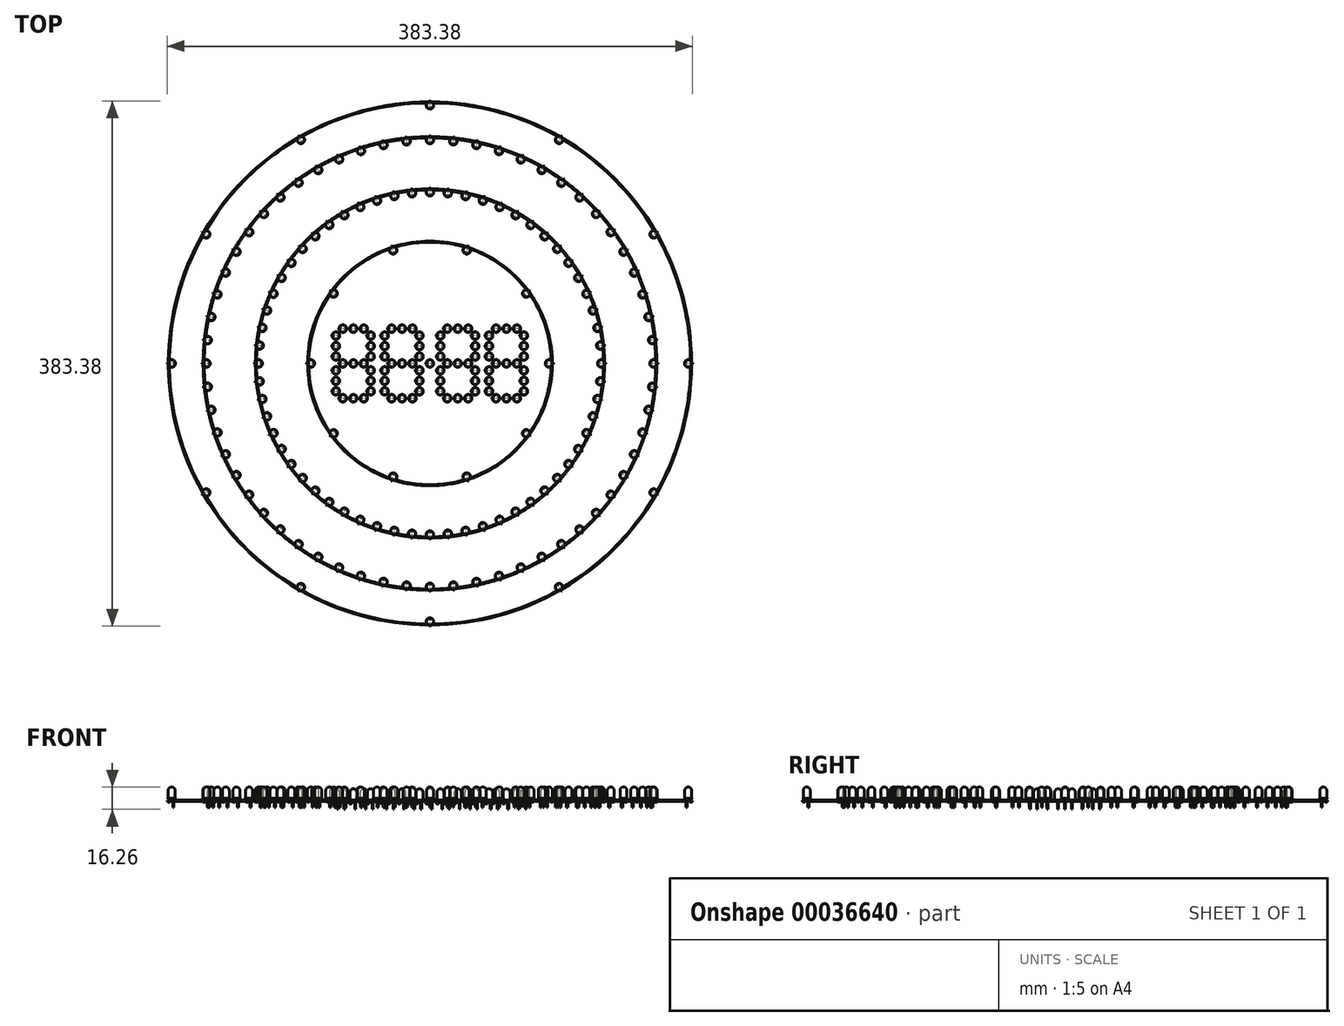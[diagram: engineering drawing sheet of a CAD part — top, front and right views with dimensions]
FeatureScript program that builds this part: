
annotation { "Feature Type Name" : "Feature", "Feature Type Description" : "" }
export const myFeature = defineFeature(function(context is Context, id is Id, definition is map)
    precondition{}
    {
        {
            var Q0;
            Q0=qCreatedBy(makeId("Top.planeOp"),FACE);
            var sketch = newSketch(context, id + "F0", { "sketchPlane" : qUnion([Q0])});
            skLineSegment(sketch, "E0", {"start": v(0, 0) * mm, "end": v(-2.8, 0) * mm});
            skLineSegment(sketch, "E1", {"start": v(-2.8, 0) * mm, "end": v(-2.8, 0.5) * mm});
            skLineSegment(sketch, "E2", {"start": v(-2.8, 0.5) * mm, "end": v(-2.54, 0.5) * mm});
            skLineSegment(sketch, "E3", {"start": v(-2.54, 0.5) * mm, "end": v(-2.54, 6.1) * mm});
            skLineSegment(sketch, "E4", {"start": v(0, 8.64) * mm, "end": v(0, 8.64) * mm});
            skLineSegment(sketch, "E5", {"start": v(0, 8.64) * mm, "end": v(0, 0) * mm});
            skPoint(sketch, "E6.visualSharp", {"position": v(-2.54, 8.64) * mm});
            skArc(sketch, "E6.filletArc", {"start": v(0, 8.64) * mm, "mid": v(-1.8, 7.9) * mm, "end": v(-2.54, 6.1) * mm});
            skSolve(sketch);
        }
        {
            var Q0;
            Q0=makeQuery(id+"F0.imprint","IMPRINT",FACE,{"disambiguationData":[TD([[makeQuery(id+"F0.imprint","IMPRINT",EDGE,{"derivedFrom":sQuery(id+"F0.wireOp",EDGE,"E0")}),-1.0]])]});
            var Q1;
            Q1=sQuery(id+"F0.wireOp",EDGE,"E5");
            revolve(context, id + "F1", {"entities" : qUnion([Q0]), "axis" : qUnion([Q1]), "revolveType" : RevolveType.FULL});
        }
        {
            var Q0;
            Q0=makeQuery(id+"F1.opRevolve","SWEPT_FACE",FACE,{"disambiguationData":[OSD([sQuery(id+"F0.wireOp",EDGE,"E0")])]});
            var sketch = newSketch(context, id + "F2", { "sketchPlane" : qUnion([Q0])});
            skLineSegment(sketch, "E7", {"start": v(0, 0) * mm, "end": v(0.89, 0) * mm, "construction": true});
            skLineSegment(sketch, "E8.bottom", {"start": v(0.89, 0.38) * mm, "end": v(1.65, 0.38) * mm});
            skLineSegment(sketch, "E8.top", {"start": v(0.89, -0.38) * mm, "end": v(1.65, -0.38) * mm});
            skLineSegment(sketch, "E8.left", {"start": v(0.89, 0.38) * mm, "end": v(0.89, -0.38) * mm});
            skLineSegment(sketch, "E8.right", {"start": v(1.65, 0.38) * mm, "end": v(1.65, -0.38) * mm});
            skLineSegment(sketch, "E9.MirrorCS", {"start": v(-0.89, 0.38) * mm, "end": v(-0.89, -0.38) * mm});
            skLineSegment(sketch, "E10.MirrorCS", {"start": v(-0.89, 0.38) * mm, "end": v(-1.65, 0.38) * mm});
            skLineSegment(sketch, "E11.MirrorCS", {"start": v(-1.65, 0.38) * mm, "end": v(-1.65, -0.38) * mm});
            skLineSegment(sketch, "E12.MirrorCS", {"start": v(-0.89, -0.38) * mm, "end": v(-1.65, -0.38) * mm});
            skSolve(sketch);
        }
        {
            var Q0;
            Q0=makeQuery(id+"F2.imprint","IMPRINT",FACE,{"disambiguationData":[TD([[makeQuery(id+"F2.imprint","IMPRINT",EDGE,{"derivedFrom":sQuery(id+"F2.wireOp",EDGE,"E9.MirrorCS")}),-1.0]])]});
            extrude(context, id + "F3", {"entities" : qUnion([Q0]), "operationType" : NewBodyOperationType.ADD, "depth" : 1.27 * mm});
        }
        {
            var Q0;
            Q0=makeQuery(id+"F2.imprint","IMPRINT",FACE,{"disambiguationData":[TD([[makeQuery(id+"F2.imprint","IMPRINT",EDGE,{"derivedFrom":sQuery(id+"F2.wireOp",EDGE,"E8.bottom")}),-1.0]])]});
            extrude(context, id + "F4", {"entities" : qUnion([Q0]), "operationType" : NewBodyOperationType.ADD, "depth" : 6.35 * mm});
        }
        {
            var Q0;
            Q0=qCreatedBy(makeId("Front.planeOp"),FACE);
            var sketch = newSketch(context, id + "F5", { "sketchPlane" : qUnion([Q0])});
            skCircle(sketch, "E13", {"center": v(-88.9, 0) * mm, "radius": 0.4 * mm});
            skCircle(sketch, "E14", {"center": v(-127, 0) * mm, "radius": 0.4 * mm});
            skCircle(sketch, "E15", {"center": v(-165.1, 0) * mm, "radius": 0.4 * mm});
            skCircle(sketch, "E16", {"center": v(-190.5, 0) * mm, "radius": 0.4 * mm});
            skLineSegment(sketch, "E17", {"start": v(0, 44.63) * mm, "end": v(0, 0) * mm, "construction": true});
            skLineSegment(sketch, "E18", {"start": v(0, 0) * mm, "end": v(0, -40.21) * mm, "construction": true});
            skSolve(sketch);
        }
        {
            var Q0;
            Q0=makeQuery(id+"F5.imprint","IMPRINT",FACE,{"disambiguationData":[TD([[makeQuery(id+"F5.imprint","IMPRINT",EDGE,{"derivedFrom":sQuery(id+"F5.wireOp",EDGE,"E16")}),1.0]])]});
            var Q1;
            Q1=makeQuery(id+"F5.imprint","IMPRINT",FACE,{"disambiguationData":[TD([[makeQuery(id+"F5.imprint","IMPRINT",EDGE,{"derivedFrom":sQuery(id+"F5.wireOp",EDGE,"E15")}),1.0]])]});
            var Q2;
            Q2=makeQuery(id+"F5.imprint","IMPRINT",FACE,{"disambiguationData":[TD([[makeQuery(id+"F5.imprint","IMPRINT",EDGE,{"derivedFrom":sQuery(id+"F5.wireOp",EDGE,"E14")}),1.0]])]});
            var Q3;
            Q3=makeQuery(id+"F5.imprint","IMPRINT",FACE,{"disambiguationData":[TD([[makeQuery(id+"F5.imprint","IMPRINT",EDGE,{"derivedFrom":sQuery(id+"F5.wireOp",EDGE,"E13")}),1.0]])]});
            var Q4;
            Q4=sQuery(id+"F5.wireOp",EDGE,"E18");
            revolve(context, id + "F6", {"entities" : qUnion([Q0, Q1, Q2, Q3]), "axis" : qUnion([Q4]), "revolveType" : RevolveType.FULL});
        }
        {
            var Q0;
            Q0=makeQuery(id+"F1.opRevolve","SWEPT_BODY",BODY,{"disambiguationData":[OSD([sQuery(id+"F0.wireOp",EDGE,"E0"),sQuery(id+"F0.wireOp",EDGE,"E1"),sQuery(id+"F0.wireOp",EDGE,"E2"),sQuery(id+"F0.wireOp",EDGE,"E3"),sQuery(id+"F0.wireOp",EDGE,"E5"),sQuery(id+"F0.wireOp",EDGE,"E6.filletArc")])]});
            var Q1;
            Q1=sQuery(id+"F0.wireOp",EDGE,"E0");
            transform(context, id + "F7", {"entities" : qUnion([Q0]), "transformType" : TransformType.ROTATION, "transformAxis" : qUnion([Q1]), "angle" : 270 * degree, "makeCopy" : false});
        }
        {
            var Q0;
            Q0=makeQuery(id+"F3.opExtrude","SWEPT_FACE",FACE,{"disambiguationData":[OSD([sQuery(id+"F2.wireOp",EDGE,"E10.MirrorCS")])]});
            var sketch = newSketch(context, id + "F8", { "sketchPlane" : qUnion([Q0])});
            skCircle(sketch, "E19", {"center": v(-2.06, -1.27) * mm, "radius": 0.4 * mm});
            skSolve(sketch);
        }
        {
            var Q0;
            Q0=makeQuery(id+"F3.opExtrude","CAP_FACE",FACE,{"disambiguationData":[OSD([sQuery(id+"F2.wireOp",EDGE,"E9.MirrorCS"),sQuery(id+"F2.wireOp",EDGE,"E10.MirrorCS"),sQuery(id+"F2.wireOp",EDGE,"E11.MirrorCS"),sQuery(id+"F2.wireOp",EDGE,"E12.MirrorCS")])],"isStart":false});
            var Q1;
            Q1=sQuery(id+"F8.wireOp",EDGE,"E19");
            revolve(context, id + "F9", {"operationType" : NewBodyOperationType.ADD, "entities" : qUnion([Q0]), "axis" : qUnion([Q1]), "revolveType" : RevolveType.ONE_DIRECTION, "oppositeDirection" : true, "angle" : 180 * degree});
        }
        {
            var Q0;
            Q0=makeQuery(id+"F1.opRevolve","SWEPT_BODY",BODY,{"disambiguationData":[OSD([sQuery(id+"F0.wireOp",EDGE,"E0"),sQuery(id+"F0.wireOp",EDGE,"E1"),sQuery(id+"F0.wireOp",EDGE,"E2"),sQuery(id+"F0.wireOp",EDGE,"E3"),sQuery(id+"F0.wireOp",EDGE,"E5"),sQuery(id+"F0.wireOp",EDGE,"E6.filletArc")])]});
            transform(context, id + "F10", {"entities" : qUnion([Q0]), "transformType" : TransformType.TRANSLATION_3D, "dx" : -86.87 * mm, "dy" : 0 * mm, "dz" : 1.27 * mm, "makeCopy" : true});
        }
        {
            var Q0;
            Q0=makeQuery(id+"F1.opRevolve","SWEPT_BODY",BODY,{"disambiguationData":[OSD([sQuery(id+"F0.wireOp",EDGE,"E0"),sQuery(id+"F0.wireOp",EDGE,"E1"),sQuery(id+"F0.wireOp",EDGE,"E2"),sQuery(id+"F0.wireOp",EDGE,"E3"),sQuery(id+"F0.wireOp",EDGE,"E5"),sQuery(id+"F0.wireOp",EDGE,"E6.filletArc")])]});
            transform(context, id + "F11", {"entities" : qUnion([Q0]), "transformType" : TransformType.TRANSLATION_3D, "dx" : -124.97 * mm, "dy" : 0 * mm, "dz" : 1.27 * mm, "makeCopy" : true});
        }
        {
            var Q0;
            Q0=makeQuery(id+"F1.opRevolve","SWEPT_BODY",BODY,{"disambiguationData":[OSD([sQuery(id+"F0.wireOp",EDGE,"E0"),sQuery(id+"F0.wireOp",EDGE,"E1"),sQuery(id+"F0.wireOp",EDGE,"E2"),sQuery(id+"F0.wireOp",EDGE,"E3"),sQuery(id+"F0.wireOp",EDGE,"E5"),sQuery(id+"F0.wireOp",EDGE,"E6.filletArc")])]});
            transform(context, id + "F12", {"entities" : qUnion([Q0]), "transformType" : TransformType.TRANSLATION_3D, "dx" : -163.07 * mm, "dy" : 0 * mm, "dz" : 1.27 * mm, "makeCopy" : true});
        }
        {
            var Q0;
            Q0=makeQuery(id+"F1.opRevolve","SWEPT_BODY",BODY,{"disambiguationData":[OSD([sQuery(id+"F0.wireOp",EDGE,"E0"),sQuery(id+"F0.wireOp",EDGE,"E1"),sQuery(id+"F0.wireOp",EDGE,"E2"),sQuery(id+"F0.wireOp",EDGE,"E3"),sQuery(id+"F0.wireOp",EDGE,"E5"),sQuery(id+"F0.wireOp",EDGE,"E6.filletArc")])]});
            transform(context, id + "F13", {"entities" : qUnion([Q0]), "transformType" : TransformType.TRANSLATION_3D, "dx" : -188.47 * mm, "dy" : 0 * mm, "dz" : 1.27 * mm, "makeCopy" : true});
        }
        {
            var Q0;
            Q0=makeQuery(id+"F10.opPattern","COPY",BODY,{"derivedFrom":makeQuery(id+"F1.opRevolve","SWEPT_BODY",BODY,{"disambiguationData":[OSD([sQuery(id+"F0.wireOp",EDGE,"E0"),sQuery(id+"F0.wireOp",EDGE,"E1"),sQuery(id+"F0.wireOp",EDGE,"E2"),sQuery(id+"F0.wireOp",EDGE,"E3"),sQuery(id+"F0.wireOp",EDGE,"E5"),sQuery(id+"F0.wireOp",EDGE,"E6.filletArc")])]}),"instanceName":"1"});
            var Q1;
            Q1=sQuery(id+"F5.wireOp",EDGE,"E17");
            circularPattern(context, id + "F14", {"entities" : qUnion([Q0]), "axis" : qUnion([Q1]), "angle" : 36 * degree, "instanceCount" : 10});
        }
        {
            var Q0;
            Q0=makeQuery(id+"F11.opPattern","COPY",BODY,{"derivedFrom":makeQuery(id+"F1.opRevolve","SWEPT_BODY",BODY,{"disambiguationData":[OSD([sQuery(id+"F0.wireOp",EDGE,"E0"),sQuery(id+"F0.wireOp",EDGE,"E1"),sQuery(id+"F0.wireOp",EDGE,"E2"),sQuery(id+"F0.wireOp",EDGE,"E3"),sQuery(id+"F0.wireOp",EDGE,"E5"),sQuery(id+"F0.wireOp",EDGE,"E6.filletArc")])]}),"instanceName":"1"});
            var Q1;
            Q1=makeQuery(id+"F12.opPattern","COPY",BODY,{"derivedFrom":makeQuery(id+"F1.opRevolve","SWEPT_BODY",BODY,{"disambiguationData":[OSD([sQuery(id+"F0.wireOp",EDGE,"E0"),sQuery(id+"F0.wireOp",EDGE,"E1"),sQuery(id+"F0.wireOp",EDGE,"E2"),sQuery(id+"F0.wireOp",EDGE,"E3"),sQuery(id+"F0.wireOp",EDGE,"E5"),sQuery(id+"F0.wireOp",EDGE,"E6.filletArc")])]}),"instanceName":"1"});
            var Q2;
            Q2=sQuery(id+"F5.wireOp",EDGE,"E17");
            circularPattern(context, id + "F15", {"entities" : qUnion([Q0, Q1]), "axis" : qUnion([Q2]), "angle" : 6 * degree, "instanceCount" : 60});
        }
        {
            var Q0;
            Q0=makeQuery(id+"F13.opPattern","COPY",BODY,{"derivedFrom":makeQuery(id+"F1.opRevolve","SWEPT_BODY",BODY,{"disambiguationData":[OSD([sQuery(id+"F0.wireOp",EDGE,"E0"),sQuery(id+"F0.wireOp",EDGE,"E1"),sQuery(id+"F0.wireOp",EDGE,"E2"),sQuery(id+"F0.wireOp",EDGE,"E3"),sQuery(id+"F0.wireOp",EDGE,"E5"),sQuery(id+"F0.wireOp",EDGE,"E6.filletArc")])]}),"instanceName":"1"});
            var Q1;
            Q1=sQuery(id+"F5.wireOp",EDGE,"E17");
            circularPattern(context, id + "F16", {"entities" : qUnion([Q0]), "axis" : qUnion([Q1]), "angle" : 30 * degree, "instanceCount" : 12});
        }
        {
            var Q0;
            Q0=makeQuery(id+"F1.opRevolve","SWEPT_BODY",BODY,{"disambiguationData":[OSD([sQuery(id+"F0.wireOp",EDGE,"E0"),sQuery(id+"F0.wireOp",EDGE,"E1"),sQuery(id+"F0.wireOp",EDGE,"E2"),sQuery(id+"F0.wireOp",EDGE,"E3"),sQuery(id+"F0.wireOp",EDGE,"E5"),sQuery(id+"F0.wireOp",EDGE,"E6.filletArc")])]});
            transform(context, id + "F17", {"entities" : qUnion([Q0]), "transformType" : TransformType.TRANSLATION_3D, "dx" : -63.5 * mm, "dy" : 0 * mm, "dz" : 0 * mm, "makeCopy" : true});
        }
        {
            var Q0;
            Q0=makeQuery(id+"F17.opPattern","COPY",BODY,{"derivedFrom":makeQuery(id+"F1.opRevolve","SWEPT_BODY",BODY,{"disambiguationData":[OSD([sQuery(id+"F0.wireOp",EDGE,"E0"),sQuery(id+"F0.wireOp",EDGE,"E1"),sQuery(id+"F0.wireOp",EDGE,"E2"),sQuery(id+"F0.wireOp",EDGE,"E3"),sQuery(id+"F0.wireOp",EDGE,"E5"),sQuery(id+"F0.wireOp",EDGE,"E6.filletArc")])]}),"instanceName":"1"});
            transform(context, id + "F18", {"entities" : qUnion([Q0]), "transformType" : TransformType.TRANSLATION_3D, "dx" : 7.62 * mm, "dy" : 0 * mm, "dz" : 0 * mm, "makeCopy" : true});
        }
        {
            var Q0;
            Q0=makeQuery(id+"F18.opPattern","COPY",BODY,{"derivedFrom":makeQuery(id+"F17.opPattern","COPY",BODY,{"derivedFrom":makeQuery(id+"F1.opRevolve","SWEPT_BODY",BODY,{"disambiguationData":[OSD([sQuery(id+"F0.wireOp",EDGE,"E0"),sQuery(id+"F0.wireOp",EDGE,"E1"),sQuery(id+"F0.wireOp",EDGE,"E2"),sQuery(id+"F0.wireOp",EDGE,"E3"),sQuery(id+"F0.wireOp",EDGE,"E5"),sQuery(id+"F0.wireOp",EDGE,"E6.filletArc")])]}),"instanceName":"1"}),"instanceName":"1"});
            transform(context, id + "F19", {"entities" : qUnion([Q0]), "transformType" : TransformType.TRANSLATION_3D, "dx" : 7.62 * mm, "dy" : 0 * mm, "dz" : 0 * mm, "makeCopy" : true});
        }
        {
            var Q0;
            Q0=makeQuery(id+"F17.opPattern","COPY",BODY,{"derivedFrom":makeQuery(id+"F1.opRevolve","SWEPT_BODY",BODY,{"disambiguationData":[OSD([sQuery(id+"F0.wireOp",EDGE,"E0"),sQuery(id+"F0.wireOp",EDGE,"E1"),sQuery(id+"F0.wireOp",EDGE,"E2"),sQuery(id+"F0.wireOp",EDGE,"E3"),sQuery(id+"F0.wireOp",EDGE,"E5"),sQuery(id+"F0.wireOp",EDGE,"E6.filletArc")])]}),"instanceName":"1"});
            var Q1;
            Q1=makeQuery(id+"F19.opPattern","COPY",BODY,{"derivedFrom":makeQuery(id+"F18.opPattern","COPY",BODY,{"derivedFrom":makeQuery(id+"F17.opPattern","COPY",BODY,{"derivedFrom":makeQuery(id+"F1.opRevolve","SWEPT_BODY",BODY,{"disambiguationData":[OSD([sQuery(id+"F0.wireOp",EDGE,"E0"),sQuery(id+"F0.wireOp",EDGE,"E1"),sQuery(id+"F0.wireOp",EDGE,"E2"),sQuery(id+"F0.wireOp",EDGE,"E3"),sQuery(id+"F0.wireOp",EDGE,"E5"),sQuery(id+"F0.wireOp",EDGE,"E6.filletArc")])]}),"instanceName":"1"}),"instanceName":"1"}),"instanceName":"1"});
            var Q2;
            Q2=makeQuery(id+"F18.opPattern","COPY",BODY,{"derivedFrom":makeQuery(id+"F17.opPattern","COPY",BODY,{"derivedFrom":makeQuery(id+"F1.opRevolve","SWEPT_BODY",BODY,{"disambiguationData":[OSD([sQuery(id+"F0.wireOp",EDGE,"E0"),sQuery(id+"F0.wireOp",EDGE,"E1"),sQuery(id+"F0.wireOp",EDGE,"E2"),sQuery(id+"F0.wireOp",EDGE,"E3"),sQuery(id+"F0.wireOp",EDGE,"E5"),sQuery(id+"F0.wireOp",EDGE,"E6.filletArc")])]}),"instanceName":"1"}),"instanceName":"1"});
            transform(context, id + "F20", {"entities" : qUnion([Q0, Q1, Q2]), "transformType" : TransformType.TRANSLATION_3D, "dx" : 0 * mm, "dy" : -25.4 * mm, "dz" : 0 * mm, "makeCopy" : true});
        }
        {
            var Q0;
            Q0=makeQuery(id+"F17.opPattern","COPY",BODY,{"derivedFrom":makeQuery(id+"F1.opRevolve","SWEPT_BODY",BODY,{"disambiguationData":[OSD([sQuery(id+"F0.wireOp",EDGE,"E0"),sQuery(id+"F0.wireOp",EDGE,"E1"),sQuery(id+"F0.wireOp",EDGE,"E2"),sQuery(id+"F0.wireOp",EDGE,"E3"),sQuery(id+"F0.wireOp",EDGE,"E5"),sQuery(id+"F0.wireOp",EDGE,"E6.filletArc")])]}),"instanceName":"1"});
            var Q1;
            Q1=makeQuery(id+"F18.opPattern","COPY",BODY,{"derivedFrom":makeQuery(id+"F17.opPattern","COPY",BODY,{"derivedFrom":makeQuery(id+"F1.opRevolve","SWEPT_BODY",BODY,{"disambiguationData":[OSD([sQuery(id+"F0.wireOp",EDGE,"E0"),sQuery(id+"F0.wireOp",EDGE,"E1"),sQuery(id+"F0.wireOp",EDGE,"E2"),sQuery(id+"F0.wireOp",EDGE,"E3"),sQuery(id+"F0.wireOp",EDGE,"E5"),sQuery(id+"F0.wireOp",EDGE,"E6.filletArc")])]}),"instanceName":"1"}),"instanceName":"1"});
            var Q2;
            Q2=makeQuery(id+"F19.opPattern","COPY",BODY,{"derivedFrom":makeQuery(id+"F18.opPattern","COPY",BODY,{"derivedFrom":makeQuery(id+"F17.opPattern","COPY",BODY,{"derivedFrom":makeQuery(id+"F1.opRevolve","SWEPT_BODY",BODY,{"disambiguationData":[OSD([sQuery(id+"F0.wireOp",EDGE,"E0"),sQuery(id+"F0.wireOp",EDGE,"E1"),sQuery(id+"F0.wireOp",EDGE,"E2"),sQuery(id+"F0.wireOp",EDGE,"E3"),sQuery(id+"F0.wireOp",EDGE,"E5"),sQuery(id+"F0.wireOp",EDGE,"E6.filletArc")])]}),"instanceName":"1"}),"instanceName":"1"}),"instanceName":"1"});
            transform(context, id + "F21", {"entities" : qUnion([Q0, Q1, Q2]), "transformType" : TransformType.TRANSLATION_3D, "dx" : 0 * mm, "dy" : 25.4 * mm, "dz" : 0 * mm, "makeCopy" : true});
        }
        {
            var Q0;
            Q0=makeQuery(id+"F1.opRevolve","SWEPT_BODY",BODY,{"disambiguationData":[OSD([sQuery(id+"F0.wireOp",EDGE,"E0"),sQuery(id+"F0.wireOp",EDGE,"E1"),sQuery(id+"F0.wireOp",EDGE,"E2"),sQuery(id+"F0.wireOp",EDGE,"E3"),sQuery(id+"F0.wireOp",EDGE,"E5"),sQuery(id+"F0.wireOp",EDGE,"E6.filletArc")])]});
            transform(context, id + "F22", {"entities" : qUnion([Q0]), "transformType" : TransformType.TRANSLATION_3D, "dx" : -68.58 * mm, "dy" : 5.08 * mm, "dz" : 0 * mm, "makeCopy" : true});
        }
        {
            var Q0;
            Q0=makeQuery(id+"F22.opPattern","COPY",BODY,{"derivedFrom":makeQuery(id+"F1.opRevolve","SWEPT_BODY",BODY,{"disambiguationData":[OSD([sQuery(id+"F0.wireOp",EDGE,"E0"),sQuery(id+"F0.wireOp",EDGE,"E1"),sQuery(id+"F0.wireOp",EDGE,"E2"),sQuery(id+"F0.wireOp",EDGE,"E3"),sQuery(id+"F0.wireOp",EDGE,"E5"),sQuery(id+"F0.wireOp",EDGE,"E6.filletArc")])]}),"instanceName":"1"});
            transform(context, id + "F23", {"entities" : qUnion([Q0]), "transformType" : TransformType.TRANSLATION_3D, "dx" : 0 * mm, "dy" : 7.62 * mm, "dz" : 0 * mm, "makeCopy" : true});
        }
        {
            var Q0;
            Q0=makeQuery(id+"F23.opPattern","COPY",BODY,{"derivedFrom":makeQuery(id+"F22.opPattern","COPY",BODY,{"derivedFrom":makeQuery(id+"F1.opRevolve","SWEPT_BODY",BODY,{"disambiguationData":[OSD([sQuery(id+"F0.wireOp",EDGE,"E0"),sQuery(id+"F0.wireOp",EDGE,"E1"),sQuery(id+"F0.wireOp",EDGE,"E2"),sQuery(id+"F0.wireOp",EDGE,"E3"),sQuery(id+"F0.wireOp",EDGE,"E5"),sQuery(id+"F0.wireOp",EDGE,"E6.filletArc")])]}),"instanceName":"1"}),"instanceName":"1"});
            transform(context, id + "F24", {"entities" : qUnion([Q0]), "transformType" : TransformType.TRANSLATION_3D, "dx" : 0 * mm, "dy" : 7.62 * mm, "dz" : 0 * mm, "makeCopy" : true});
        }
        {
            var Q0;
            Q0=makeQuery(id+"F24.opPattern","COPY",BODY,{"derivedFrom":makeQuery(id+"F23.opPattern","COPY",BODY,{"derivedFrom":makeQuery(id+"F22.opPattern","COPY",BODY,{"derivedFrom":makeQuery(id+"F1.opRevolve","SWEPT_BODY",BODY,{"disambiguationData":[OSD([sQuery(id+"F0.wireOp",EDGE,"E0"),sQuery(id+"F0.wireOp",EDGE,"E1"),sQuery(id+"F0.wireOp",EDGE,"E2"),sQuery(id+"F0.wireOp",EDGE,"E3"),sQuery(id+"F0.wireOp",EDGE,"E5"),sQuery(id+"F0.wireOp",EDGE,"E6.filletArc")])]}),"instanceName":"1"}),"instanceName":"1"}),"instanceName":"1"});
            var Q1;
            Q1=makeQuery(id+"F23.opPattern","COPY",BODY,{"derivedFrom":makeQuery(id+"F22.opPattern","COPY",BODY,{"derivedFrom":makeQuery(id+"F1.opRevolve","SWEPT_BODY",BODY,{"disambiguationData":[OSD([sQuery(id+"F0.wireOp",EDGE,"E0"),sQuery(id+"F0.wireOp",EDGE,"E1"),sQuery(id+"F0.wireOp",EDGE,"E2"),sQuery(id+"F0.wireOp",EDGE,"E3"),sQuery(id+"F0.wireOp",EDGE,"E5"),sQuery(id+"F0.wireOp",EDGE,"E6.filletArc")])]}),"instanceName":"1"}),"instanceName":"1"});
            var Q2;
            Q2=makeQuery(id+"F22.opPattern","COPY",BODY,{"derivedFrom":makeQuery(id+"F1.opRevolve","SWEPT_BODY",BODY,{"disambiguationData":[OSD([sQuery(id+"F0.wireOp",EDGE,"E0"),sQuery(id+"F0.wireOp",EDGE,"E1"),sQuery(id+"F0.wireOp",EDGE,"E2"),sQuery(id+"F0.wireOp",EDGE,"E3"),sQuery(id+"F0.wireOp",EDGE,"E5"),sQuery(id+"F0.wireOp",EDGE,"E6.filletArc")])]}),"instanceName":"1"});
            transform(context, id + "F25", {"entities" : qUnion([Q0, Q1, Q2]), "transformType" : TransformType.TRANSLATION_3D, "dx" : 25.4 * mm, "dy" : 0 * mm, "dz" : 0 * mm, "makeCopy" : true});
        }
        {
            var Q0;
            Q0=makeQuery(id+"F25.opPattern","COPY",BODY,{"derivedFrom":makeQuery(id+"F24.opPattern","COPY",BODY,{"derivedFrom":makeQuery(id+"F23.opPattern","COPY",BODY,{"derivedFrom":makeQuery(id+"F22.opPattern","COPY",BODY,{"derivedFrom":makeQuery(id+"F1.opRevolve","SWEPT_BODY",BODY,{"disambiguationData":[OSD([sQuery(id+"F0.wireOp",EDGE,"E0"),sQuery(id+"F0.wireOp",EDGE,"E1"),sQuery(id+"F0.wireOp",EDGE,"E2"),sQuery(id+"F0.wireOp",EDGE,"E3"),sQuery(id+"F0.wireOp",EDGE,"E5"),sQuery(id+"F0.wireOp",EDGE,"E6.filletArc")])]}),"instanceName":"1"}),"instanceName":"1"}),"instanceName":"1"}),"instanceName":"1"});
            var Q1;
            Q1=makeQuery(id+"F25.opPattern","COPY",BODY,{"derivedFrom":makeQuery(id+"F23.opPattern","COPY",BODY,{"derivedFrom":makeQuery(id+"F22.opPattern","COPY",BODY,{"derivedFrom":makeQuery(id+"F1.opRevolve","SWEPT_BODY",BODY,{"disambiguationData":[OSD([sQuery(id+"F0.wireOp",EDGE,"E0"),sQuery(id+"F0.wireOp",EDGE,"E1"),sQuery(id+"F0.wireOp",EDGE,"E2"),sQuery(id+"F0.wireOp",EDGE,"E3"),sQuery(id+"F0.wireOp",EDGE,"E5"),sQuery(id+"F0.wireOp",EDGE,"E6.filletArc")])]}),"instanceName":"1"}),"instanceName":"1"}),"instanceName":"1"});
            var Q2;
            Q2=makeQuery(id+"F25.opPattern","COPY",BODY,{"derivedFrom":makeQuery(id+"F22.opPattern","COPY",BODY,{"derivedFrom":makeQuery(id+"F1.opRevolve","SWEPT_BODY",BODY,{"disambiguationData":[OSD([sQuery(id+"F0.wireOp",EDGE,"E0"),sQuery(id+"F0.wireOp",EDGE,"E1"),sQuery(id+"F0.wireOp",EDGE,"E2"),sQuery(id+"F0.wireOp",EDGE,"E3"),sQuery(id+"F0.wireOp",EDGE,"E5"),sQuery(id+"F0.wireOp",EDGE,"E6.filletArc")])]}),"instanceName":"1"}),"instanceName":"1"});
            var Q3;
            Q3=makeQuery(id+"F22.opPattern","COPY",BODY,{"derivedFrom":makeQuery(id+"F1.opRevolve","SWEPT_BODY",BODY,{"disambiguationData":[OSD([sQuery(id+"F0.wireOp",EDGE,"E0"),sQuery(id+"F0.wireOp",EDGE,"E1"),sQuery(id+"F0.wireOp",EDGE,"E2"),sQuery(id+"F0.wireOp",EDGE,"E3"),sQuery(id+"F0.wireOp",EDGE,"E5"),sQuery(id+"F0.wireOp",EDGE,"E6.filletArc")])]}),"instanceName":"1"});
            var Q4;
            Q4=makeQuery(id+"F23.opPattern","COPY",BODY,{"derivedFrom":makeQuery(id+"F22.opPattern","COPY",BODY,{"derivedFrom":makeQuery(id+"F1.opRevolve","SWEPT_BODY",BODY,{"disambiguationData":[OSD([sQuery(id+"F0.wireOp",EDGE,"E0"),sQuery(id+"F0.wireOp",EDGE,"E1"),sQuery(id+"F0.wireOp",EDGE,"E2"),sQuery(id+"F0.wireOp",EDGE,"E3"),sQuery(id+"F0.wireOp",EDGE,"E5"),sQuery(id+"F0.wireOp",EDGE,"E6.filletArc")])]}),"instanceName":"1"}),"instanceName":"1"});
            var Q5;
            Q5=makeQuery(id+"F24.opPattern","COPY",BODY,{"derivedFrom":makeQuery(id+"F23.opPattern","COPY",BODY,{"derivedFrom":makeQuery(id+"F22.opPattern","COPY",BODY,{"derivedFrom":makeQuery(id+"F1.opRevolve","SWEPT_BODY",BODY,{"disambiguationData":[OSD([sQuery(id+"F0.wireOp",EDGE,"E0"),sQuery(id+"F0.wireOp",EDGE,"E1"),sQuery(id+"F0.wireOp",EDGE,"E2"),sQuery(id+"F0.wireOp",EDGE,"E3"),sQuery(id+"F0.wireOp",EDGE,"E5"),sQuery(id+"F0.wireOp",EDGE,"E6.filletArc")])]}),"instanceName":"1"}),"instanceName":"1"}),"instanceName":"1"});
            transform(context, id + "F26", {"entities" : qUnion([Q0, Q1, Q2, Q3, Q4, Q5]), "transformType" : TransformType.TRANSLATION_3D, "dx" : 0 * mm, "dy" : -25.4 * mm, "dz" : 0 * mm, "makeCopy" : true});
        }
        {
            var Q0;
            Q0=makeQuery(id+"F21.opPattern","COPY",BODY,{"derivedFrom":makeQuery(id+"F17.opPattern","COPY",BODY,{"derivedFrom":makeQuery(id+"F1.opRevolve","SWEPT_BODY",BODY,{"disambiguationData":[OSD([sQuery(id+"F0.wireOp",EDGE,"E0"),sQuery(id+"F0.wireOp",EDGE,"E1"),sQuery(id+"F0.wireOp",EDGE,"E2"),sQuery(id+"F0.wireOp",EDGE,"E3"),sQuery(id+"F0.wireOp",EDGE,"E5"),sQuery(id+"F0.wireOp",EDGE,"E6.filletArc")])]}),"instanceName":"1"}),"instanceName":"1"});
            var Q1;
            Q1=makeQuery(id+"F25.opPattern","COPY",BODY,{"derivedFrom":makeQuery(id+"F24.opPattern","COPY",BODY,{"derivedFrom":makeQuery(id+"F23.opPattern","COPY",BODY,{"derivedFrom":makeQuery(id+"F22.opPattern","COPY",BODY,{"derivedFrom":makeQuery(id+"F1.opRevolve","SWEPT_BODY",BODY,{"disambiguationData":[OSD([sQuery(id+"F0.wireOp",EDGE,"E0"),sQuery(id+"F0.wireOp",EDGE,"E1"),sQuery(id+"F0.wireOp",EDGE,"E2"),sQuery(id+"F0.wireOp",EDGE,"E3"),sQuery(id+"F0.wireOp",EDGE,"E5"),sQuery(id+"F0.wireOp",EDGE,"E6.filletArc")])]}),"instanceName":"1"}),"instanceName":"1"}),"instanceName":"1"}),"instanceName":"1"});
            var Q2;
            Q2=makeQuery(id+"F25.opPattern","COPY",BODY,{"derivedFrom":makeQuery(id+"F23.opPattern","COPY",BODY,{"derivedFrom":makeQuery(id+"F22.opPattern","COPY",BODY,{"derivedFrom":makeQuery(id+"F1.opRevolve","SWEPT_BODY",BODY,{"disambiguationData":[OSD([sQuery(id+"F0.wireOp",EDGE,"E0"),sQuery(id+"F0.wireOp",EDGE,"E1"),sQuery(id+"F0.wireOp",EDGE,"E2"),sQuery(id+"F0.wireOp",EDGE,"E3"),sQuery(id+"F0.wireOp",EDGE,"E5"),sQuery(id+"F0.wireOp",EDGE,"E6.filletArc")])]}),"instanceName":"1"}),"instanceName":"1"}),"instanceName":"1"});
            var Q3;
            Q3=makeQuery(id+"F25.opPattern","COPY",BODY,{"derivedFrom":makeQuery(id+"F22.opPattern","COPY",BODY,{"derivedFrom":makeQuery(id+"F1.opRevolve","SWEPT_BODY",BODY,{"disambiguationData":[OSD([sQuery(id+"F0.wireOp",EDGE,"E0"),sQuery(id+"F0.wireOp",EDGE,"E1"),sQuery(id+"F0.wireOp",EDGE,"E2"),sQuery(id+"F0.wireOp",EDGE,"E3"),sQuery(id+"F0.wireOp",EDGE,"E5"),sQuery(id+"F0.wireOp",EDGE,"E6.filletArc")])]}),"instanceName":"1"}),"instanceName":"1"});
            var Q4;
            Q4=makeQuery(id+"F19.opPattern","COPY",BODY,{"derivedFrom":makeQuery(id+"F18.opPattern","COPY",BODY,{"derivedFrom":makeQuery(id+"F17.opPattern","COPY",BODY,{"derivedFrom":makeQuery(id+"F1.opRevolve","SWEPT_BODY",BODY,{"disambiguationData":[OSD([sQuery(id+"F0.wireOp",EDGE,"E0"),sQuery(id+"F0.wireOp",EDGE,"E1"),sQuery(id+"F0.wireOp",EDGE,"E2"),sQuery(id+"F0.wireOp",EDGE,"E3"),sQuery(id+"F0.wireOp",EDGE,"E5"),sQuery(id+"F0.wireOp",EDGE,"E6.filletArc")])]}),"instanceName":"1"}),"instanceName":"1"}),"instanceName":"1"});
            var Q5;
            Q5=makeQuery(id+"F18.opPattern","COPY",BODY,{"derivedFrom":makeQuery(id+"F17.opPattern","COPY",BODY,{"derivedFrom":makeQuery(id+"F1.opRevolve","SWEPT_BODY",BODY,{"disambiguationData":[OSD([sQuery(id+"F0.wireOp",EDGE,"E0"),sQuery(id+"F0.wireOp",EDGE,"E1"),sQuery(id+"F0.wireOp",EDGE,"E2"),sQuery(id+"F0.wireOp",EDGE,"E3"),sQuery(id+"F0.wireOp",EDGE,"E5"),sQuery(id+"F0.wireOp",EDGE,"E6.filletArc")])]}),"instanceName":"1"}),"instanceName":"1"});
            var Q6;
            Q6=makeQuery(id+"F17.opPattern","COPY",BODY,{"derivedFrom":makeQuery(id+"F1.opRevolve","SWEPT_BODY",BODY,{"disambiguationData":[OSD([sQuery(id+"F0.wireOp",EDGE,"E0"),sQuery(id+"F0.wireOp",EDGE,"E1"),sQuery(id+"F0.wireOp",EDGE,"E2"),sQuery(id+"F0.wireOp",EDGE,"E3"),sQuery(id+"F0.wireOp",EDGE,"E5"),sQuery(id+"F0.wireOp",EDGE,"E6.filletArc")])]}),"instanceName":"1"});
            var Q7;
            Q7=makeQuery(id+"F22.opPattern","COPY",BODY,{"derivedFrom":makeQuery(id+"F1.opRevolve","SWEPT_BODY",BODY,{"disambiguationData":[OSD([sQuery(id+"F0.wireOp",EDGE,"E0"),sQuery(id+"F0.wireOp",EDGE,"E1"),sQuery(id+"F0.wireOp",EDGE,"E2"),sQuery(id+"F0.wireOp",EDGE,"E3"),sQuery(id+"F0.wireOp",EDGE,"E5"),sQuery(id+"F0.wireOp",EDGE,"E6.filletArc")])]}),"instanceName":"1"});
            var Q8;
            Q8=makeQuery(id+"F23.opPattern","COPY",BODY,{"derivedFrom":makeQuery(id+"F22.opPattern","COPY",BODY,{"derivedFrom":makeQuery(id+"F1.opRevolve","SWEPT_BODY",BODY,{"disambiguationData":[OSD([sQuery(id+"F0.wireOp",EDGE,"E0"),sQuery(id+"F0.wireOp",EDGE,"E1"),sQuery(id+"F0.wireOp",EDGE,"E2"),sQuery(id+"F0.wireOp",EDGE,"E3"),sQuery(id+"F0.wireOp",EDGE,"E5"),sQuery(id+"F0.wireOp",EDGE,"E6.filletArc")])]}),"instanceName":"1"}),"instanceName":"1"});
            var Q9;
            Q9=makeQuery(id+"F24.opPattern","COPY",BODY,{"derivedFrom":makeQuery(id+"F23.opPattern","COPY",BODY,{"derivedFrom":makeQuery(id+"F22.opPattern","COPY",BODY,{"derivedFrom":makeQuery(id+"F1.opRevolve","SWEPT_BODY",BODY,{"disambiguationData":[OSD([sQuery(id+"F0.wireOp",EDGE,"E0"),sQuery(id+"F0.wireOp",EDGE,"E1"),sQuery(id+"F0.wireOp",EDGE,"E2"),sQuery(id+"F0.wireOp",EDGE,"E3"),sQuery(id+"F0.wireOp",EDGE,"E5"),sQuery(id+"F0.wireOp",EDGE,"E6.filletArc")])]}),"instanceName":"1"}),"instanceName":"1"}),"instanceName":"1"});
            var Q10;
            Q10=makeQuery(id+"F21.opPattern","COPY",BODY,{"derivedFrom":makeQuery(id+"F19.opPattern","COPY",BODY,{"derivedFrom":makeQuery(id+"F18.opPattern","COPY",BODY,{"derivedFrom":makeQuery(id+"F17.opPattern","COPY",BODY,{"derivedFrom":makeQuery(id+"F1.opRevolve","SWEPT_BODY",BODY,{"disambiguationData":[OSD([sQuery(id+"F0.wireOp",EDGE,"E0"),sQuery(id+"F0.wireOp",EDGE,"E1"),sQuery(id+"F0.wireOp",EDGE,"E2"),sQuery(id+"F0.wireOp",EDGE,"E3"),sQuery(id+"F0.wireOp",EDGE,"E5"),sQuery(id+"F0.wireOp",EDGE,"E6.filletArc")])]}),"instanceName":"1"}),"instanceName":"1"}),"instanceName":"1"}),"instanceName":"1"});
            var Q11;
            Q11=makeQuery(id+"F20.opPattern","COPY",BODY,{"derivedFrom":makeQuery(id+"F19.opPattern","COPY",BODY,{"derivedFrom":makeQuery(id+"F18.opPattern","COPY",BODY,{"derivedFrom":makeQuery(id+"F17.opPattern","COPY",BODY,{"derivedFrom":makeQuery(id+"F1.opRevolve","SWEPT_BODY",BODY,{"disambiguationData":[OSD([sQuery(id+"F0.wireOp",EDGE,"E0"),sQuery(id+"F0.wireOp",EDGE,"E1"),sQuery(id+"F0.wireOp",EDGE,"E2"),sQuery(id+"F0.wireOp",EDGE,"E3"),sQuery(id+"F0.wireOp",EDGE,"E5"),sQuery(id+"F0.wireOp",EDGE,"E6.filletArc")])]}),"instanceName":"1"}),"instanceName":"1"}),"instanceName":"1"}),"instanceName":"1"});
            var Q12;
            Q12=makeQuery(id+"F20.opPattern","COPY",BODY,{"derivedFrom":makeQuery(id+"F18.opPattern","COPY",BODY,{"derivedFrom":makeQuery(id+"F17.opPattern","COPY",BODY,{"derivedFrom":makeQuery(id+"F1.opRevolve","SWEPT_BODY",BODY,{"disambiguationData":[OSD([sQuery(id+"F0.wireOp",EDGE,"E0"),sQuery(id+"F0.wireOp",EDGE,"E1"),sQuery(id+"F0.wireOp",EDGE,"E2"),sQuery(id+"F0.wireOp",EDGE,"E3"),sQuery(id+"F0.wireOp",EDGE,"E5"),sQuery(id+"F0.wireOp",EDGE,"E6.filletArc")])]}),"instanceName":"1"}),"instanceName":"1"}),"instanceName":"1"});
            var Q13;
            Q13=makeQuery(id+"F20.opPattern","COPY",BODY,{"derivedFrom":makeQuery(id+"F17.opPattern","COPY",BODY,{"derivedFrom":makeQuery(id+"F1.opRevolve","SWEPT_BODY",BODY,{"disambiguationData":[OSD([sQuery(id+"F0.wireOp",EDGE,"E0"),sQuery(id+"F0.wireOp",EDGE,"E1"),sQuery(id+"F0.wireOp",EDGE,"E2"),sQuery(id+"F0.wireOp",EDGE,"E3"),sQuery(id+"F0.wireOp",EDGE,"E5"),sQuery(id+"F0.wireOp",EDGE,"E6.filletArc")])]}),"instanceName":"1"}),"instanceName":"1"});
            var Q14;
            Q14=makeQuery(id+"F21.opPattern","COPY",BODY,{"derivedFrom":makeQuery(id+"F18.opPattern","COPY",BODY,{"derivedFrom":makeQuery(id+"F17.opPattern","COPY",BODY,{"derivedFrom":makeQuery(id+"F1.opRevolve","SWEPT_BODY",BODY,{"disambiguationData":[OSD([sQuery(id+"F0.wireOp",EDGE,"E0"),sQuery(id+"F0.wireOp",EDGE,"E1"),sQuery(id+"F0.wireOp",EDGE,"E2"),sQuery(id+"F0.wireOp",EDGE,"E3"),sQuery(id+"F0.wireOp",EDGE,"E5"),sQuery(id+"F0.wireOp",EDGE,"E6.filletArc")])]}),"instanceName":"1"}),"instanceName":"1"}),"instanceName":"1"});
            var Q15;
            Q15=makeQuery(id+"F26.opPattern","COPY",BODY,{"derivedFrom":makeQuery(id+"F25.opPattern","COPY",BODY,{"derivedFrom":makeQuery(id+"F24.opPattern","COPY",BODY,{"derivedFrom":makeQuery(id+"F23.opPattern","COPY",BODY,{"derivedFrom":makeQuery(id+"F22.opPattern","COPY",BODY,{"derivedFrom":makeQuery(id+"F1.opRevolve","SWEPT_BODY",BODY,{"disambiguationData":[OSD([sQuery(id+"F0.wireOp",EDGE,"E0"),sQuery(id+"F0.wireOp",EDGE,"E1"),sQuery(id+"F0.wireOp",EDGE,"E2"),sQuery(id+"F0.wireOp",EDGE,"E3"),sQuery(id+"F0.wireOp",EDGE,"E5"),sQuery(id+"F0.wireOp",EDGE,"E6.filletArc")])]}),"instanceName":"1"}),"instanceName":"1"}),"instanceName":"1"}),"instanceName":"1"}),"instanceName":"1"});
            var Q16;
            Q16=makeQuery(id+"F26.opPattern","COPY",BODY,{"derivedFrom":makeQuery(id+"F25.opPattern","COPY",BODY,{"derivedFrom":makeQuery(id+"F23.opPattern","COPY",BODY,{"derivedFrom":makeQuery(id+"F22.opPattern","COPY",BODY,{"derivedFrom":makeQuery(id+"F1.opRevolve","SWEPT_BODY",BODY,{"disambiguationData":[OSD([sQuery(id+"F0.wireOp",EDGE,"E0"),sQuery(id+"F0.wireOp",EDGE,"E1"),sQuery(id+"F0.wireOp",EDGE,"E2"),sQuery(id+"F0.wireOp",EDGE,"E3"),sQuery(id+"F0.wireOp",EDGE,"E5"),sQuery(id+"F0.wireOp",EDGE,"E6.filletArc")])]}),"instanceName":"1"}),"instanceName":"1"}),"instanceName":"1"}),"instanceName":"1"});
            var Q17;
            Q17=makeQuery(id+"F26.opPattern","COPY",BODY,{"derivedFrom":makeQuery(id+"F25.opPattern","COPY",BODY,{"derivedFrom":makeQuery(id+"F22.opPattern","COPY",BODY,{"derivedFrom":makeQuery(id+"F1.opRevolve","SWEPT_BODY",BODY,{"disambiguationData":[OSD([sQuery(id+"F0.wireOp",EDGE,"E0"),sQuery(id+"F0.wireOp",EDGE,"E1"),sQuery(id+"F0.wireOp",EDGE,"E2"),sQuery(id+"F0.wireOp",EDGE,"E3"),sQuery(id+"F0.wireOp",EDGE,"E5"),sQuery(id+"F0.wireOp",EDGE,"E6.filletArc")])]}),"instanceName":"1"}),"instanceName":"1"}),"instanceName":"1"});
            var Q18;
            Q18=makeQuery(id+"F26.opPattern","COPY",BODY,{"derivedFrom":makeQuery(id+"F22.opPattern","COPY",BODY,{"derivedFrom":makeQuery(id+"F1.opRevolve","SWEPT_BODY",BODY,{"disambiguationData":[OSD([sQuery(id+"F0.wireOp",EDGE,"E0"),sQuery(id+"F0.wireOp",EDGE,"E1"),sQuery(id+"F0.wireOp",EDGE,"E2"),sQuery(id+"F0.wireOp",EDGE,"E3"),sQuery(id+"F0.wireOp",EDGE,"E5"),sQuery(id+"F0.wireOp",EDGE,"E6.filletArc")])]}),"instanceName":"1"}),"instanceName":"1"});
            var Q19;
            Q19=makeQuery(id+"F26.opPattern","COPY",BODY,{"derivedFrom":makeQuery(id+"F24.opPattern","COPY",BODY,{"derivedFrom":makeQuery(id+"F23.opPattern","COPY",BODY,{"derivedFrom":makeQuery(id+"F22.opPattern","COPY",BODY,{"derivedFrom":makeQuery(id+"F1.opRevolve","SWEPT_BODY",BODY,{"disambiguationData":[OSD([sQuery(id+"F0.wireOp",EDGE,"E0"),sQuery(id+"F0.wireOp",EDGE,"E1"),sQuery(id+"F0.wireOp",EDGE,"E2"),sQuery(id+"F0.wireOp",EDGE,"E3"),sQuery(id+"F0.wireOp",EDGE,"E5"),sQuery(id+"F0.wireOp",EDGE,"E6.filletArc")])]}),"instanceName":"1"}),"instanceName":"1"}),"instanceName":"1"}),"instanceName":"1"});
            var Q20;
            Q20=makeQuery(id+"F26.opPattern","COPY",BODY,{"derivedFrom":makeQuery(id+"F23.opPattern","COPY",BODY,{"derivedFrom":makeQuery(id+"F22.opPattern","COPY",BODY,{"derivedFrom":makeQuery(id+"F1.opRevolve","SWEPT_BODY",BODY,{"disambiguationData":[OSD([sQuery(id+"F0.wireOp",EDGE,"E0"),sQuery(id+"F0.wireOp",EDGE,"E1"),sQuery(id+"F0.wireOp",EDGE,"E2"),sQuery(id+"F0.wireOp",EDGE,"E3"),sQuery(id+"F0.wireOp",EDGE,"E5"),sQuery(id+"F0.wireOp",EDGE,"E6.filletArc")])]}),"instanceName":"1"}),"instanceName":"1"}),"instanceName":"1"});
            transform(context, id + "F27", {"entities" : qUnion([Q0, Q1, Q2, Q3, Q4, Q5, Q6, Q7, Q8, Q9, Q10, Q11, Q12, Q13, Q14, Q15, Q16, Q17, Q18, Q19, Q20]), "transformType" : TransformType.TRANSLATION_3D, "dx" : 35.56 * mm, "dy" : 0 * mm, "dz" : 0 * mm, "makeCopy" : true});
        }
        {
            var Q0;
            Q0=makeQuery(id+"F18.opPattern","COPY",BODY,{"derivedFrom":makeQuery(id+"F17.opPattern","COPY",BODY,{"derivedFrom":makeQuery(id+"F1.opRevolve","SWEPT_BODY",BODY,{"disambiguationData":[OSD([sQuery(id+"F0.wireOp",EDGE,"E0"),sQuery(id+"F0.wireOp",EDGE,"E1"),sQuery(id+"F0.wireOp",EDGE,"E2"),sQuery(id+"F0.wireOp",EDGE,"E3"),sQuery(id+"F0.wireOp",EDGE,"E5"),sQuery(id+"F0.wireOp",EDGE,"E6.filletArc")])]}),"instanceName":"1"}),"instanceName":"1"});
            var Q1;
            Q1=makeQuery(id+"F17.opPattern","COPY",BODY,{"derivedFrom":makeQuery(id+"F1.opRevolve","SWEPT_BODY",BODY,{"disambiguationData":[OSD([sQuery(id+"F0.wireOp",EDGE,"E0"),sQuery(id+"F0.wireOp",EDGE,"E1"),sQuery(id+"F0.wireOp",EDGE,"E2"),sQuery(id+"F0.wireOp",EDGE,"E3"),sQuery(id+"F0.wireOp",EDGE,"E5"),sQuery(id+"F0.wireOp",EDGE,"E6.filletArc")])]}),"instanceName":"1"});
            var Q2;
            Q2=makeQuery(id+"F19.opPattern","COPY",BODY,{"derivedFrom":makeQuery(id+"F18.opPattern","COPY",BODY,{"derivedFrom":makeQuery(id+"F17.opPattern","COPY",BODY,{"derivedFrom":makeQuery(id+"F1.opRevolve","SWEPT_BODY",BODY,{"disambiguationData":[OSD([sQuery(id+"F0.wireOp",EDGE,"E0"),sQuery(id+"F0.wireOp",EDGE,"E1"),sQuery(id+"F0.wireOp",EDGE,"E2"),sQuery(id+"F0.wireOp",EDGE,"E3"),sQuery(id+"F0.wireOp",EDGE,"E5"),sQuery(id+"F0.wireOp",EDGE,"E6.filletArc")])]}),"instanceName":"1"}),"instanceName":"1"}),"instanceName":"1"});
            var Q3;
            Q3=makeQuery(id+"F20.opPattern","COPY",BODY,{"derivedFrom":makeQuery(id+"F18.opPattern","COPY",BODY,{"derivedFrom":makeQuery(id+"F17.opPattern","COPY",BODY,{"derivedFrom":makeQuery(id+"F1.opRevolve","SWEPT_BODY",BODY,{"disambiguationData":[OSD([sQuery(id+"F0.wireOp",EDGE,"E0"),sQuery(id+"F0.wireOp",EDGE,"E1"),sQuery(id+"F0.wireOp",EDGE,"E2"),sQuery(id+"F0.wireOp",EDGE,"E3"),sQuery(id+"F0.wireOp",EDGE,"E5"),sQuery(id+"F0.wireOp",EDGE,"E6.filletArc")])]}),"instanceName":"1"}),"instanceName":"1"}),"instanceName":"1"});
            var Q4;
            Q4=makeQuery(id+"F20.opPattern","COPY",BODY,{"derivedFrom":makeQuery(id+"F19.opPattern","COPY",BODY,{"derivedFrom":makeQuery(id+"F18.opPattern","COPY",BODY,{"derivedFrom":makeQuery(id+"F17.opPattern","COPY",BODY,{"derivedFrom":makeQuery(id+"F1.opRevolve","SWEPT_BODY",BODY,{"disambiguationData":[OSD([sQuery(id+"F0.wireOp",EDGE,"E0"),sQuery(id+"F0.wireOp",EDGE,"E1"),sQuery(id+"F0.wireOp",EDGE,"E2"),sQuery(id+"F0.wireOp",EDGE,"E3"),sQuery(id+"F0.wireOp",EDGE,"E5"),sQuery(id+"F0.wireOp",EDGE,"E6.filletArc")])]}),"instanceName":"1"}),"instanceName":"1"}),"instanceName":"1"}),"instanceName":"1"});
            var Q5;
            Q5=makeQuery(id+"F20.opPattern","COPY",BODY,{"derivedFrom":makeQuery(id+"F17.opPattern","COPY",BODY,{"derivedFrom":makeQuery(id+"F1.opRevolve","SWEPT_BODY",BODY,{"disambiguationData":[OSD([sQuery(id+"F0.wireOp",EDGE,"E0"),sQuery(id+"F0.wireOp",EDGE,"E1"),sQuery(id+"F0.wireOp",EDGE,"E2"),sQuery(id+"F0.wireOp",EDGE,"E3"),sQuery(id+"F0.wireOp",EDGE,"E5"),sQuery(id+"F0.wireOp",EDGE,"E6.filletArc")])]}),"instanceName":"1"}),"instanceName":"1"});
            var Q6;
            Q6=makeQuery(id+"F21.opPattern","COPY",BODY,{"derivedFrom":makeQuery(id+"F19.opPattern","COPY",BODY,{"derivedFrom":makeQuery(id+"F18.opPattern","COPY",BODY,{"derivedFrom":makeQuery(id+"F17.opPattern","COPY",BODY,{"derivedFrom":makeQuery(id+"F1.opRevolve","SWEPT_BODY",BODY,{"disambiguationData":[OSD([sQuery(id+"F0.wireOp",EDGE,"E0"),sQuery(id+"F0.wireOp",EDGE,"E1"),sQuery(id+"F0.wireOp",EDGE,"E2"),sQuery(id+"F0.wireOp",EDGE,"E3"),sQuery(id+"F0.wireOp",EDGE,"E5"),sQuery(id+"F0.wireOp",EDGE,"E6.filletArc")])]}),"instanceName":"1"}),"instanceName":"1"}),"instanceName":"1"}),"instanceName":"1"});
            var Q7;
            Q7=makeQuery(id+"F21.opPattern","COPY",BODY,{"derivedFrom":makeQuery(id+"F18.opPattern","COPY",BODY,{"derivedFrom":makeQuery(id+"F17.opPattern","COPY",BODY,{"derivedFrom":makeQuery(id+"F1.opRevolve","SWEPT_BODY",BODY,{"disambiguationData":[OSD([sQuery(id+"F0.wireOp",EDGE,"E0"),sQuery(id+"F0.wireOp",EDGE,"E1"),sQuery(id+"F0.wireOp",EDGE,"E2"),sQuery(id+"F0.wireOp",EDGE,"E3"),sQuery(id+"F0.wireOp",EDGE,"E5"),sQuery(id+"F0.wireOp",EDGE,"E6.filletArc")])]}),"instanceName":"1"}),"instanceName":"1"}),"instanceName":"1"});
            var Q8;
            Q8=makeQuery(id+"F21.opPattern","COPY",BODY,{"derivedFrom":makeQuery(id+"F17.opPattern","COPY",BODY,{"derivedFrom":makeQuery(id+"F1.opRevolve","SWEPT_BODY",BODY,{"disambiguationData":[OSD([sQuery(id+"F0.wireOp",EDGE,"E0"),sQuery(id+"F0.wireOp",EDGE,"E1"),sQuery(id+"F0.wireOp",EDGE,"E2"),sQuery(id+"F0.wireOp",EDGE,"E3"),sQuery(id+"F0.wireOp",EDGE,"E5"),sQuery(id+"F0.wireOp",EDGE,"E6.filletArc")])]}),"instanceName":"1"}),"instanceName":"1"});
            var Q9;
            Q9=makeQuery(id+"F22.opPattern","COPY",BODY,{"derivedFrom":makeQuery(id+"F1.opRevolve","SWEPT_BODY",BODY,{"disambiguationData":[OSD([sQuery(id+"F0.wireOp",EDGE,"E0"),sQuery(id+"F0.wireOp",EDGE,"E1"),sQuery(id+"F0.wireOp",EDGE,"E2"),sQuery(id+"F0.wireOp",EDGE,"E3"),sQuery(id+"F0.wireOp",EDGE,"E5"),sQuery(id+"F0.wireOp",EDGE,"E6.filletArc")])]}),"instanceName":"1"});
            var Q10;
            Q10=makeQuery(id+"F23.opPattern","COPY",BODY,{"derivedFrom":makeQuery(id+"F22.opPattern","COPY",BODY,{"derivedFrom":makeQuery(id+"F1.opRevolve","SWEPT_BODY",BODY,{"disambiguationData":[OSD([sQuery(id+"F0.wireOp",EDGE,"E0"),sQuery(id+"F0.wireOp",EDGE,"E1"),sQuery(id+"F0.wireOp",EDGE,"E2"),sQuery(id+"F0.wireOp",EDGE,"E3"),sQuery(id+"F0.wireOp",EDGE,"E5"),sQuery(id+"F0.wireOp",EDGE,"E6.filletArc")])]}),"instanceName":"1"}),"instanceName":"1"});
            var Q11;
            Q11=makeQuery(id+"F24.opPattern","COPY",BODY,{"derivedFrom":makeQuery(id+"F23.opPattern","COPY",BODY,{"derivedFrom":makeQuery(id+"F22.opPattern","COPY",BODY,{"derivedFrom":makeQuery(id+"F1.opRevolve","SWEPT_BODY",BODY,{"disambiguationData":[OSD([sQuery(id+"F0.wireOp",EDGE,"E0"),sQuery(id+"F0.wireOp",EDGE,"E1"),sQuery(id+"F0.wireOp",EDGE,"E2"),sQuery(id+"F0.wireOp",EDGE,"E3"),sQuery(id+"F0.wireOp",EDGE,"E5"),sQuery(id+"F0.wireOp",EDGE,"E6.filletArc")])]}),"instanceName":"1"}),"instanceName":"1"}),"instanceName":"1"});
            var Q12;
            Q12=makeQuery(id+"F25.opPattern","COPY",BODY,{"derivedFrom":makeQuery(id+"F24.opPattern","COPY",BODY,{"derivedFrom":makeQuery(id+"F23.opPattern","COPY",BODY,{"derivedFrom":makeQuery(id+"F22.opPattern","COPY",BODY,{"derivedFrom":makeQuery(id+"F1.opRevolve","SWEPT_BODY",BODY,{"disambiguationData":[OSD([sQuery(id+"F0.wireOp",EDGE,"E0"),sQuery(id+"F0.wireOp",EDGE,"E1"),sQuery(id+"F0.wireOp",EDGE,"E2"),sQuery(id+"F0.wireOp",EDGE,"E3"),sQuery(id+"F0.wireOp",EDGE,"E5"),sQuery(id+"F0.wireOp",EDGE,"E6.filletArc")])]}),"instanceName":"1"}),"instanceName":"1"}),"instanceName":"1"}),"instanceName":"1"});
            var Q13;
            Q13=makeQuery(id+"F25.opPattern","COPY",BODY,{"derivedFrom":makeQuery(id+"F23.opPattern","COPY",BODY,{"derivedFrom":makeQuery(id+"F22.opPattern","COPY",BODY,{"derivedFrom":makeQuery(id+"F1.opRevolve","SWEPT_BODY",BODY,{"disambiguationData":[OSD([sQuery(id+"F0.wireOp",EDGE,"E0"),sQuery(id+"F0.wireOp",EDGE,"E1"),sQuery(id+"F0.wireOp",EDGE,"E2"),sQuery(id+"F0.wireOp",EDGE,"E3"),sQuery(id+"F0.wireOp",EDGE,"E5"),sQuery(id+"F0.wireOp",EDGE,"E6.filletArc")])]}),"instanceName":"1"}),"instanceName":"1"}),"instanceName":"1"});
            var Q14;
            Q14=makeQuery(id+"F25.opPattern","COPY",BODY,{"derivedFrom":makeQuery(id+"F22.opPattern","COPY",BODY,{"derivedFrom":makeQuery(id+"F1.opRevolve","SWEPT_BODY",BODY,{"disambiguationData":[OSD([sQuery(id+"F0.wireOp",EDGE,"E0"),sQuery(id+"F0.wireOp",EDGE,"E1"),sQuery(id+"F0.wireOp",EDGE,"E2"),sQuery(id+"F0.wireOp",EDGE,"E3"),sQuery(id+"F0.wireOp",EDGE,"E5"),sQuery(id+"F0.wireOp",EDGE,"E6.filletArc")])]}),"instanceName":"1"}),"instanceName":"1"});
            var Q15;
            Q15=makeQuery(id+"F26.opPattern","COPY",BODY,{"derivedFrom":makeQuery(id+"F25.opPattern","COPY",BODY,{"derivedFrom":makeQuery(id+"F24.opPattern","COPY",BODY,{"derivedFrom":makeQuery(id+"F23.opPattern","COPY",BODY,{"derivedFrom":makeQuery(id+"F22.opPattern","COPY",BODY,{"derivedFrom":makeQuery(id+"F1.opRevolve","SWEPT_BODY",BODY,{"disambiguationData":[OSD([sQuery(id+"F0.wireOp",EDGE,"E0"),sQuery(id+"F0.wireOp",EDGE,"E1"),sQuery(id+"F0.wireOp",EDGE,"E2"),sQuery(id+"F0.wireOp",EDGE,"E3"),sQuery(id+"F0.wireOp",EDGE,"E5"),sQuery(id+"F0.wireOp",EDGE,"E6.filletArc")])]}),"instanceName":"1"}),"instanceName":"1"}),"instanceName":"1"}),"instanceName":"1"}),"instanceName":"1"});
            var Q16;
            Q16=makeQuery(id+"F26.opPattern","COPY",BODY,{"derivedFrom":makeQuery(id+"F25.opPattern","COPY",BODY,{"derivedFrom":makeQuery(id+"F23.opPattern","COPY",BODY,{"derivedFrom":makeQuery(id+"F22.opPattern","COPY",BODY,{"derivedFrom":makeQuery(id+"F1.opRevolve","SWEPT_BODY",BODY,{"disambiguationData":[OSD([sQuery(id+"F0.wireOp",EDGE,"E0"),sQuery(id+"F0.wireOp",EDGE,"E1"),sQuery(id+"F0.wireOp",EDGE,"E2"),sQuery(id+"F0.wireOp",EDGE,"E3"),sQuery(id+"F0.wireOp",EDGE,"E5"),sQuery(id+"F0.wireOp",EDGE,"E6.filletArc")])]}),"instanceName":"1"}),"instanceName":"1"}),"instanceName":"1"}),"instanceName":"1"});
            var Q17;
            Q17=makeQuery(id+"F26.opPattern","COPY",BODY,{"derivedFrom":makeQuery(id+"F25.opPattern","COPY",BODY,{"derivedFrom":makeQuery(id+"F22.opPattern","COPY",BODY,{"derivedFrom":makeQuery(id+"F1.opRevolve","SWEPT_BODY",BODY,{"disambiguationData":[OSD([sQuery(id+"F0.wireOp",EDGE,"E0"),sQuery(id+"F0.wireOp",EDGE,"E1"),sQuery(id+"F0.wireOp",EDGE,"E2"),sQuery(id+"F0.wireOp",EDGE,"E3"),sQuery(id+"F0.wireOp",EDGE,"E5"),sQuery(id+"F0.wireOp",EDGE,"E6.filletArc")])]}),"instanceName":"1"}),"instanceName":"1"}),"instanceName":"1"});
            var Q18;
            Q18=makeQuery(id+"F26.opPattern","COPY",BODY,{"derivedFrom":makeQuery(id+"F24.opPattern","COPY",BODY,{"derivedFrom":makeQuery(id+"F23.opPattern","COPY",BODY,{"derivedFrom":makeQuery(id+"F22.opPattern","COPY",BODY,{"derivedFrom":makeQuery(id+"F1.opRevolve","SWEPT_BODY",BODY,{"disambiguationData":[OSD([sQuery(id+"F0.wireOp",EDGE,"E0"),sQuery(id+"F0.wireOp",EDGE,"E1"),sQuery(id+"F0.wireOp",EDGE,"E2"),sQuery(id+"F0.wireOp",EDGE,"E3"),sQuery(id+"F0.wireOp",EDGE,"E5"),sQuery(id+"F0.wireOp",EDGE,"E6.filletArc")])]}),"instanceName":"1"}),"instanceName":"1"}),"instanceName":"1"}),"instanceName":"1"});
            var Q19;
            Q19=makeQuery(id+"F26.opPattern","COPY",BODY,{"derivedFrom":makeQuery(id+"F23.opPattern","COPY",BODY,{"derivedFrom":makeQuery(id+"F22.opPattern","COPY",BODY,{"derivedFrom":makeQuery(id+"F1.opRevolve","SWEPT_BODY",BODY,{"disambiguationData":[OSD([sQuery(id+"F0.wireOp",EDGE,"E0"),sQuery(id+"F0.wireOp",EDGE,"E1"),sQuery(id+"F0.wireOp",EDGE,"E2"),sQuery(id+"F0.wireOp",EDGE,"E3"),sQuery(id+"F0.wireOp",EDGE,"E5"),sQuery(id+"F0.wireOp",EDGE,"E6.filletArc")])]}),"instanceName":"1"}),"instanceName":"1"}),"instanceName":"1"});
            var Q20;
            Q20=makeQuery(id+"F26.opPattern","COPY",BODY,{"derivedFrom":makeQuery(id+"F22.opPattern","COPY",BODY,{"derivedFrom":makeQuery(id+"F1.opRevolve","SWEPT_BODY",BODY,{"disambiguationData":[OSD([sQuery(id+"F0.wireOp",EDGE,"E0"),sQuery(id+"F0.wireOp",EDGE,"E1"),sQuery(id+"F0.wireOp",EDGE,"E2"),sQuery(id+"F0.wireOp",EDGE,"E3"),sQuery(id+"F0.wireOp",EDGE,"E5"),sQuery(id+"F0.wireOp",EDGE,"E6.filletArc")])]}),"instanceName":"1"}),"instanceName":"1"});
            var Q21;
            Q21=makeQuery(id+"F27.opPattern","COPY",BODY,{"derivedFrom":makeQuery(id+"F20.opPattern","COPY",BODY,{"derivedFrom":makeQuery(id+"F18.opPattern","COPY",BODY,{"derivedFrom":makeQuery(id+"F17.opPattern","COPY",BODY,{"derivedFrom":makeQuery(id+"F1.opRevolve","SWEPT_BODY",BODY,{"disambiguationData":[OSD([sQuery(id+"F0.wireOp",EDGE,"E0"),sQuery(id+"F0.wireOp",EDGE,"E1"),sQuery(id+"F0.wireOp",EDGE,"E2"),sQuery(id+"F0.wireOp",EDGE,"E3"),sQuery(id+"F0.wireOp",EDGE,"E5"),sQuery(id+"F0.wireOp",EDGE,"E6.filletArc")])]}),"instanceName":"1"}),"instanceName":"1"}),"instanceName":"1"}),"instanceName":"1"});
            var Q22;
            Q22=makeQuery(id+"F27.opPattern","COPY",BODY,{"derivedFrom":makeQuery(id+"F20.opPattern","COPY",BODY,{"derivedFrom":makeQuery(id+"F17.opPattern","COPY",BODY,{"derivedFrom":makeQuery(id+"F1.opRevolve","SWEPT_BODY",BODY,{"disambiguationData":[OSD([sQuery(id+"F0.wireOp",EDGE,"E0"),sQuery(id+"F0.wireOp",EDGE,"E1"),sQuery(id+"F0.wireOp",EDGE,"E2"),sQuery(id+"F0.wireOp",EDGE,"E3"),sQuery(id+"F0.wireOp",EDGE,"E5"),sQuery(id+"F0.wireOp",EDGE,"E6.filletArc")])]}),"instanceName":"1"}),"instanceName":"1"}),"instanceName":"1"});
            var Q23;
            Q23=makeQuery(id+"F27.opPattern","COPY",BODY,{"derivedFrom":makeQuery(id+"F21.opPattern","COPY",BODY,{"derivedFrom":makeQuery(id+"F18.opPattern","COPY",BODY,{"derivedFrom":makeQuery(id+"F17.opPattern","COPY",BODY,{"derivedFrom":makeQuery(id+"F1.opRevolve","SWEPT_BODY",BODY,{"disambiguationData":[OSD([sQuery(id+"F0.wireOp",EDGE,"E0"),sQuery(id+"F0.wireOp",EDGE,"E1"),sQuery(id+"F0.wireOp",EDGE,"E2"),sQuery(id+"F0.wireOp",EDGE,"E3"),sQuery(id+"F0.wireOp",EDGE,"E5"),sQuery(id+"F0.wireOp",EDGE,"E6.filletArc")])]}),"instanceName":"1"}),"instanceName":"1"}),"instanceName":"1"}),"instanceName":"1"});
            var Q24;
            Q24=makeQuery(id+"F27.opPattern","COPY",BODY,{"derivedFrom":makeQuery(id+"F21.opPattern","COPY",BODY,{"derivedFrom":makeQuery(id+"F17.opPattern","COPY",BODY,{"derivedFrom":makeQuery(id+"F1.opRevolve","SWEPT_BODY",BODY,{"disambiguationData":[OSD([sQuery(id+"F0.wireOp",EDGE,"E0"),sQuery(id+"F0.wireOp",EDGE,"E1"),sQuery(id+"F0.wireOp",EDGE,"E2"),sQuery(id+"F0.wireOp",EDGE,"E3"),sQuery(id+"F0.wireOp",EDGE,"E5"),sQuery(id+"F0.wireOp",EDGE,"E6.filletArc")])]}),"instanceName":"1"}),"instanceName":"1"}),"instanceName":"1"});
            var Q25;
            Q25=makeQuery(id+"F27.opPattern","COPY",BODY,{"derivedFrom":makeQuery(id+"F20.opPattern","COPY",BODY,{"derivedFrom":makeQuery(id+"F19.opPattern","COPY",BODY,{"derivedFrom":makeQuery(id+"F18.opPattern","COPY",BODY,{"derivedFrom":makeQuery(id+"F17.opPattern","COPY",BODY,{"derivedFrom":makeQuery(id+"F1.opRevolve","SWEPT_BODY",BODY,{"disambiguationData":[OSD([sQuery(id+"F0.wireOp",EDGE,"E0"),sQuery(id+"F0.wireOp",EDGE,"E1"),sQuery(id+"F0.wireOp",EDGE,"E2"),sQuery(id+"F0.wireOp",EDGE,"E3"),sQuery(id+"F0.wireOp",EDGE,"E5"),sQuery(id+"F0.wireOp",EDGE,"E6.filletArc")])]}),"instanceName":"1"}),"instanceName":"1"}),"instanceName":"1"}),"instanceName":"1"}),"instanceName":"1"});
            var Q26;
            Q26=makeQuery(id+"F27.opPattern","COPY",BODY,{"derivedFrom":makeQuery(id+"F21.opPattern","COPY",BODY,{"derivedFrom":makeQuery(id+"F19.opPattern","COPY",BODY,{"derivedFrom":makeQuery(id+"F18.opPattern","COPY",BODY,{"derivedFrom":makeQuery(id+"F17.opPattern","COPY",BODY,{"derivedFrom":makeQuery(id+"F1.opRevolve","SWEPT_BODY",BODY,{"disambiguationData":[OSD([sQuery(id+"F0.wireOp",EDGE,"E0"),sQuery(id+"F0.wireOp",EDGE,"E1"),sQuery(id+"F0.wireOp",EDGE,"E2"),sQuery(id+"F0.wireOp",EDGE,"E3"),sQuery(id+"F0.wireOp",EDGE,"E5"),sQuery(id+"F0.wireOp",EDGE,"E6.filletArc")])]}),"instanceName":"1"}),"instanceName":"1"}),"instanceName":"1"}),"instanceName":"1"}),"instanceName":"1"});
            var Q27;
            Q27=makeQuery(id+"F27.opPattern","COPY",BODY,{"derivedFrom":makeQuery(id+"F26.opPattern","COPY",BODY,{"derivedFrom":makeQuery(id+"F25.opPattern","COPY",BODY,{"derivedFrom":makeQuery(id+"F23.opPattern","COPY",BODY,{"derivedFrom":makeQuery(id+"F22.opPattern","COPY",BODY,{"derivedFrom":makeQuery(id+"F1.opRevolve","SWEPT_BODY",BODY,{"disambiguationData":[OSD([sQuery(id+"F0.wireOp",EDGE,"E0"),sQuery(id+"F0.wireOp",EDGE,"E1"),sQuery(id+"F0.wireOp",EDGE,"E2"),sQuery(id+"F0.wireOp",EDGE,"E3"),sQuery(id+"F0.wireOp",EDGE,"E5"),sQuery(id+"F0.wireOp",EDGE,"E6.filletArc")])]}),"instanceName":"1"}),"instanceName":"1"}),"instanceName":"1"}),"instanceName":"1"}),"instanceName":"1"});
            var Q28;
            Q28=makeQuery(id+"F27.opPattern","COPY",BODY,{"derivedFrom":makeQuery(id+"F26.opPattern","COPY",BODY,{"derivedFrom":makeQuery(id+"F25.opPattern","COPY",BODY,{"derivedFrom":makeQuery(id+"F24.opPattern","COPY",BODY,{"derivedFrom":makeQuery(id+"F23.opPattern","COPY",BODY,{"derivedFrom":makeQuery(id+"F22.opPattern","COPY",BODY,{"derivedFrom":makeQuery(id+"F1.opRevolve","SWEPT_BODY",BODY,{"disambiguationData":[OSD([sQuery(id+"F0.wireOp",EDGE,"E0"),sQuery(id+"F0.wireOp",EDGE,"E1"),sQuery(id+"F0.wireOp",EDGE,"E2"),sQuery(id+"F0.wireOp",EDGE,"E3"),sQuery(id+"F0.wireOp",EDGE,"E5"),sQuery(id+"F0.wireOp",EDGE,"E6.filletArc")])]}),"instanceName":"1"}),"instanceName":"1"}),"instanceName":"1"}),"instanceName":"1"}),"instanceName":"1"}),"instanceName":"1"});
            var Q29;
            Q29=makeQuery(id+"F27.opPattern","COPY",BODY,{"derivedFrom":makeQuery(id+"F19.opPattern","COPY",BODY,{"derivedFrom":makeQuery(id+"F18.opPattern","COPY",BODY,{"derivedFrom":makeQuery(id+"F17.opPattern","COPY",BODY,{"derivedFrom":makeQuery(id+"F1.opRevolve","SWEPT_BODY",BODY,{"disambiguationData":[OSD([sQuery(id+"F0.wireOp",EDGE,"E0"),sQuery(id+"F0.wireOp",EDGE,"E1"),sQuery(id+"F0.wireOp",EDGE,"E2"),sQuery(id+"F0.wireOp",EDGE,"E3"),sQuery(id+"F0.wireOp",EDGE,"E5"),sQuery(id+"F0.wireOp",EDGE,"E6.filletArc")])]}),"instanceName":"1"}),"instanceName":"1"}),"instanceName":"1"}),"instanceName":"1"});
            var Q30;
            Q30=makeQuery(id+"F27.opPattern","COPY",BODY,{"derivedFrom":makeQuery(id+"F24.opPattern","COPY",BODY,{"derivedFrom":makeQuery(id+"F23.opPattern","COPY",BODY,{"derivedFrom":makeQuery(id+"F22.opPattern","COPY",BODY,{"derivedFrom":makeQuery(id+"F1.opRevolve","SWEPT_BODY",BODY,{"disambiguationData":[OSD([sQuery(id+"F0.wireOp",EDGE,"E0"),sQuery(id+"F0.wireOp",EDGE,"E1"),sQuery(id+"F0.wireOp",EDGE,"E2"),sQuery(id+"F0.wireOp",EDGE,"E3"),sQuery(id+"F0.wireOp",EDGE,"E5"),sQuery(id+"F0.wireOp",EDGE,"E6.filletArc")])]}),"instanceName":"1"}),"instanceName":"1"}),"instanceName":"1"}),"instanceName":"1"});
            var Q31;
            Q31=makeQuery(id+"F27.opPattern","COPY",BODY,{"derivedFrom":makeQuery(id+"F23.opPattern","COPY",BODY,{"derivedFrom":makeQuery(id+"F22.opPattern","COPY",BODY,{"derivedFrom":makeQuery(id+"F1.opRevolve","SWEPT_BODY",BODY,{"disambiguationData":[OSD([sQuery(id+"F0.wireOp",EDGE,"E0"),sQuery(id+"F0.wireOp",EDGE,"E1"),sQuery(id+"F0.wireOp",EDGE,"E2"),sQuery(id+"F0.wireOp",EDGE,"E3"),sQuery(id+"F0.wireOp",EDGE,"E5"),sQuery(id+"F0.wireOp",EDGE,"E6.filletArc")])]}),"instanceName":"1"}),"instanceName":"1"}),"instanceName":"1"});
            var Q32;
            Q32=makeQuery(id+"F27.opPattern","COPY",BODY,{"derivedFrom":makeQuery(id+"F26.opPattern","COPY",BODY,{"derivedFrom":makeQuery(id+"F25.opPattern","COPY",BODY,{"derivedFrom":makeQuery(id+"F22.opPattern","COPY",BODY,{"derivedFrom":makeQuery(id+"F1.opRevolve","SWEPT_BODY",BODY,{"disambiguationData":[OSD([sQuery(id+"F0.wireOp",EDGE,"E0"),sQuery(id+"F0.wireOp",EDGE,"E1"),sQuery(id+"F0.wireOp",EDGE,"E2"),sQuery(id+"F0.wireOp",EDGE,"E3"),sQuery(id+"F0.wireOp",EDGE,"E5"),sQuery(id+"F0.wireOp",EDGE,"E6.filletArc")])]}),"instanceName":"1"}),"instanceName":"1"}),"instanceName":"1"}),"instanceName":"1"});
            var Q33;
            Q33=makeQuery(id+"F27.opPattern","COPY",BODY,{"derivedFrom":makeQuery(id+"F22.opPattern","COPY",BODY,{"derivedFrom":makeQuery(id+"F1.opRevolve","SWEPT_BODY",BODY,{"disambiguationData":[OSD([sQuery(id+"F0.wireOp",EDGE,"E0"),sQuery(id+"F0.wireOp",EDGE,"E1"),sQuery(id+"F0.wireOp",EDGE,"E2"),sQuery(id+"F0.wireOp",EDGE,"E3"),sQuery(id+"F0.wireOp",EDGE,"E5"),sQuery(id+"F0.wireOp",EDGE,"E6.filletArc")])]}),"instanceName":"1"}),"instanceName":"1"});
            var Q34;
            Q34=makeQuery(id+"F27.opPattern","COPY",BODY,{"derivedFrom":makeQuery(id+"F25.opPattern","COPY",BODY,{"derivedFrom":makeQuery(id+"F22.opPattern","COPY",BODY,{"derivedFrom":makeQuery(id+"F1.opRevolve","SWEPT_BODY",BODY,{"disambiguationData":[OSD([sQuery(id+"F0.wireOp",EDGE,"E0"),sQuery(id+"F0.wireOp",EDGE,"E1"),sQuery(id+"F0.wireOp",EDGE,"E2"),sQuery(id+"F0.wireOp",EDGE,"E3"),sQuery(id+"F0.wireOp",EDGE,"E5"),sQuery(id+"F0.wireOp",EDGE,"E6.filletArc")])]}),"instanceName":"1"}),"instanceName":"1"}),"instanceName":"1"});
            var Q35;
            Q35=makeQuery(id+"F27.opPattern","COPY",BODY,{"derivedFrom":makeQuery(id+"F18.opPattern","COPY",BODY,{"derivedFrom":makeQuery(id+"F17.opPattern","COPY",BODY,{"derivedFrom":makeQuery(id+"F1.opRevolve","SWEPT_BODY",BODY,{"disambiguationData":[OSD([sQuery(id+"F0.wireOp",EDGE,"E0"),sQuery(id+"F0.wireOp",EDGE,"E1"),sQuery(id+"F0.wireOp",EDGE,"E2"),sQuery(id+"F0.wireOp",EDGE,"E3"),sQuery(id+"F0.wireOp",EDGE,"E5"),sQuery(id+"F0.wireOp",EDGE,"E6.filletArc")])]}),"instanceName":"1"}),"instanceName":"1"}),"instanceName":"1"});
            var Q36;
            Q36=makeQuery(id+"F27.opPattern","COPY",BODY,{"derivedFrom":makeQuery(id+"F25.opPattern","COPY",BODY,{"derivedFrom":makeQuery(id+"F24.opPattern","COPY",BODY,{"derivedFrom":makeQuery(id+"F23.opPattern","COPY",BODY,{"derivedFrom":makeQuery(id+"F22.opPattern","COPY",BODY,{"derivedFrom":makeQuery(id+"F1.opRevolve","SWEPT_BODY",BODY,{"disambiguationData":[OSD([sQuery(id+"F0.wireOp",EDGE,"E0"),sQuery(id+"F0.wireOp",EDGE,"E1"),sQuery(id+"F0.wireOp",EDGE,"E2"),sQuery(id+"F0.wireOp",EDGE,"E3"),sQuery(id+"F0.wireOp",EDGE,"E5"),sQuery(id+"F0.wireOp",EDGE,"E6.filletArc")])]}),"instanceName":"1"}),"instanceName":"1"}),"instanceName":"1"}),"instanceName":"1"}),"instanceName":"1"});
            var Q37;
            Q37=makeQuery(id+"F27.opPattern","COPY",BODY,{"derivedFrom":makeQuery(id+"F25.opPattern","COPY",BODY,{"derivedFrom":makeQuery(id+"F23.opPattern","COPY",BODY,{"derivedFrom":makeQuery(id+"F22.opPattern","COPY",BODY,{"derivedFrom":makeQuery(id+"F1.opRevolve","SWEPT_BODY",BODY,{"disambiguationData":[OSD([sQuery(id+"F0.wireOp",EDGE,"E0"),sQuery(id+"F0.wireOp",EDGE,"E1"),sQuery(id+"F0.wireOp",EDGE,"E2"),sQuery(id+"F0.wireOp",EDGE,"E3"),sQuery(id+"F0.wireOp",EDGE,"E5"),sQuery(id+"F0.wireOp",EDGE,"E6.filletArc")])]}),"instanceName":"1"}),"instanceName":"1"}),"instanceName":"1"}),"instanceName":"1"});
            var Q38;
            Q38=makeQuery(id+"F27.opPattern","COPY",BODY,{"derivedFrom":makeQuery(id+"F26.opPattern","COPY",BODY,{"derivedFrom":makeQuery(id+"F22.opPattern","COPY",BODY,{"derivedFrom":makeQuery(id+"F1.opRevolve","SWEPT_BODY",BODY,{"disambiguationData":[OSD([sQuery(id+"F0.wireOp",EDGE,"E0"),sQuery(id+"F0.wireOp",EDGE,"E1"),sQuery(id+"F0.wireOp",EDGE,"E2"),sQuery(id+"F0.wireOp",EDGE,"E3"),sQuery(id+"F0.wireOp",EDGE,"E5"),sQuery(id+"F0.wireOp",EDGE,"E6.filletArc")])]}),"instanceName":"1"}),"instanceName":"1"}),"instanceName":"1"});
            var Q39;
            Q39=makeQuery(id+"F27.opPattern","COPY",BODY,{"derivedFrom":makeQuery(id+"F17.opPattern","COPY",BODY,{"derivedFrom":makeQuery(id+"F1.opRevolve","SWEPT_BODY",BODY,{"disambiguationData":[OSD([sQuery(id+"F0.wireOp",EDGE,"E0"),sQuery(id+"F0.wireOp",EDGE,"E1"),sQuery(id+"F0.wireOp",EDGE,"E2"),sQuery(id+"F0.wireOp",EDGE,"E3"),sQuery(id+"F0.wireOp",EDGE,"E5"),sQuery(id+"F0.wireOp",EDGE,"E6.filletArc")])]}),"instanceName":"1"}),"instanceName":"1"});
            var Q40;
            Q40=makeQuery(id+"F27.opPattern","COPY",BODY,{"derivedFrom":makeQuery(id+"F26.opPattern","COPY",BODY,{"derivedFrom":makeQuery(id+"F23.opPattern","COPY",BODY,{"derivedFrom":makeQuery(id+"F22.opPattern","COPY",BODY,{"derivedFrom":makeQuery(id+"F1.opRevolve","SWEPT_BODY",BODY,{"disambiguationData":[OSD([sQuery(id+"F0.wireOp",EDGE,"E0"),sQuery(id+"F0.wireOp",EDGE,"E1"),sQuery(id+"F0.wireOp",EDGE,"E2"),sQuery(id+"F0.wireOp",EDGE,"E3"),sQuery(id+"F0.wireOp",EDGE,"E5"),sQuery(id+"F0.wireOp",EDGE,"E6.filletArc")])]}),"instanceName":"1"}),"instanceName":"1"}),"instanceName":"1"}),"instanceName":"1"});
            var Q41;
            Q41=makeQuery(id+"F27.opPattern","COPY",BODY,{"derivedFrom":makeQuery(id+"F26.opPattern","COPY",BODY,{"derivedFrom":makeQuery(id+"F24.opPattern","COPY",BODY,{"derivedFrom":makeQuery(id+"F23.opPattern","COPY",BODY,{"derivedFrom":makeQuery(id+"F22.opPattern","COPY",BODY,{"derivedFrom":makeQuery(id+"F1.opRevolve","SWEPT_BODY",BODY,{"disambiguationData":[OSD([sQuery(id+"F0.wireOp",EDGE,"E0"),sQuery(id+"F0.wireOp",EDGE,"E1"),sQuery(id+"F0.wireOp",EDGE,"E2"),sQuery(id+"F0.wireOp",EDGE,"E3"),sQuery(id+"F0.wireOp",EDGE,"E5"),sQuery(id+"F0.wireOp",EDGE,"E6.filletArc")])]}),"instanceName":"1"}),"instanceName":"1"}),"instanceName":"1"}),"instanceName":"1"}),"instanceName":"1"});
            transform(context, id + "F28", {"entities" : qUnion([Q0, Q1, Q2, Q3, Q4, Q5, Q6, Q7, Q8, Q9, Q10, Q11, Q12, Q13, Q14, Q15, Q16, Q17, Q18, Q19, Q20, Q21, Q22, Q23, Q24, Q25, Q26, Q27, Q28, Q29, Q30, Q31, Q32, Q33, Q34, Q35, Q36, Q37, Q38, Q39, Q40, Q41]), "transformType" : TransformType.TRANSLATION_3D, "dx" : 76.2 * mm, "dy" : 0 * mm, "dz" : 0 * mm, "makeCopy" : true});
        }
    });
